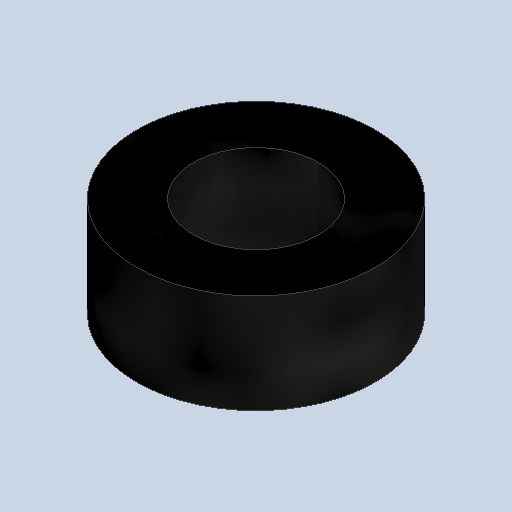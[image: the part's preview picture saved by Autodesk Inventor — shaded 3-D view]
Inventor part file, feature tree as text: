
AUTODESK INVENTOR PART (.ipt)
format: ipt  version: 2024.2 (Build 282272000, 272)  size: 240,640 bytes
history: native  units: mm
features: revolve x1, sketch x1
ambient origin geometry x8: Origin, YZ Plane, XZ Plane, XY Plane, X Axis, Y Axis, Z Axis, Center Point
bodies: Solid1 (feature_tree)
feature tree (2):
  revolve  "Revolution1"  [1 undecoded]
  sketch  "Sketch1"  dims[d5=90.0deg]
note: 1 required parameter value undecoded (feature->parameter linkage not recoverable at this tier; creation-order binding heuristic only, values carry confidence <= 0.55)
